# Revit family: LENSES-S-2000-DA840-SEN-TP-USB
name_source: partatom
category: Oprawy oświetleniowe
revit_build: Autodesk Revit 2017 (Build: 20190507_1515(x64)
units: mm (PartAtom-declared; Revit-internal decimal feet)

## family parameters
Numer OmniClass = 23.80.70.11
Obiekt nadrzędny = Powierzchnia
Punkt obliczania pomieszczeń = Nie
Tnij formami wycięć po wczytaniu = Nie
Typ części = Normalny
Tytuł OmniClass = Luminaries for Internal Lighting
Współdzielony = Nie
Wymiar okrągłego złącza = Użyj średnicy
Źródło światła = Tak

## types (1)
- LENSES-S 2000/DA840 SEN-TP-USB
    Domyślna rzędna = 0 mm  [stored 0 ft]
    Emituj kształt widoczny w renderingu = Nie
    Emituj z długości prostokąta = 289 mm  [stored 0.948163 ft]
    Emituj z szerokości prostokąta = 515 mm  [stored 1.68963 ft]
    Filtr koloru = 16777215
    Kod zespołu = D5020200
    Lampa = LED
    Model = 0637493
    Obciążenie pozorne = 130 VA
    Odchylenie kierunku = 90.00°
    Plik sieci fotometrycznej = LENSES-S 2000DA840.IES
    Producent = RIDI Leuchten GmbH
    URL = www.spectral-lighting.com
    Zmiana temperatury barwowej przyciemniania lampy = <Brak>
    brand = RIDI
    conformity mark = CE
    electrical safety class = 1
    height = 1950 mm  [stored 6.39764 ft]
    ingress protection (IP) code = IP20
    length = 515 mm  [stored 1.68963 ft]
    nominal frequency = 50-60Hz
    nominal voltage = 230
    product name = LENSES-S 2000/DA840 SEN-TP-USB
    rated input power = 130
    voltage type (AC, DC, UC) = AC
    weight = 16 kg
    width = 330 mm

note: [stored X ft] marks values corroborated as IEEE doubles in the binary element streams (Revit-internal decimal feet)
